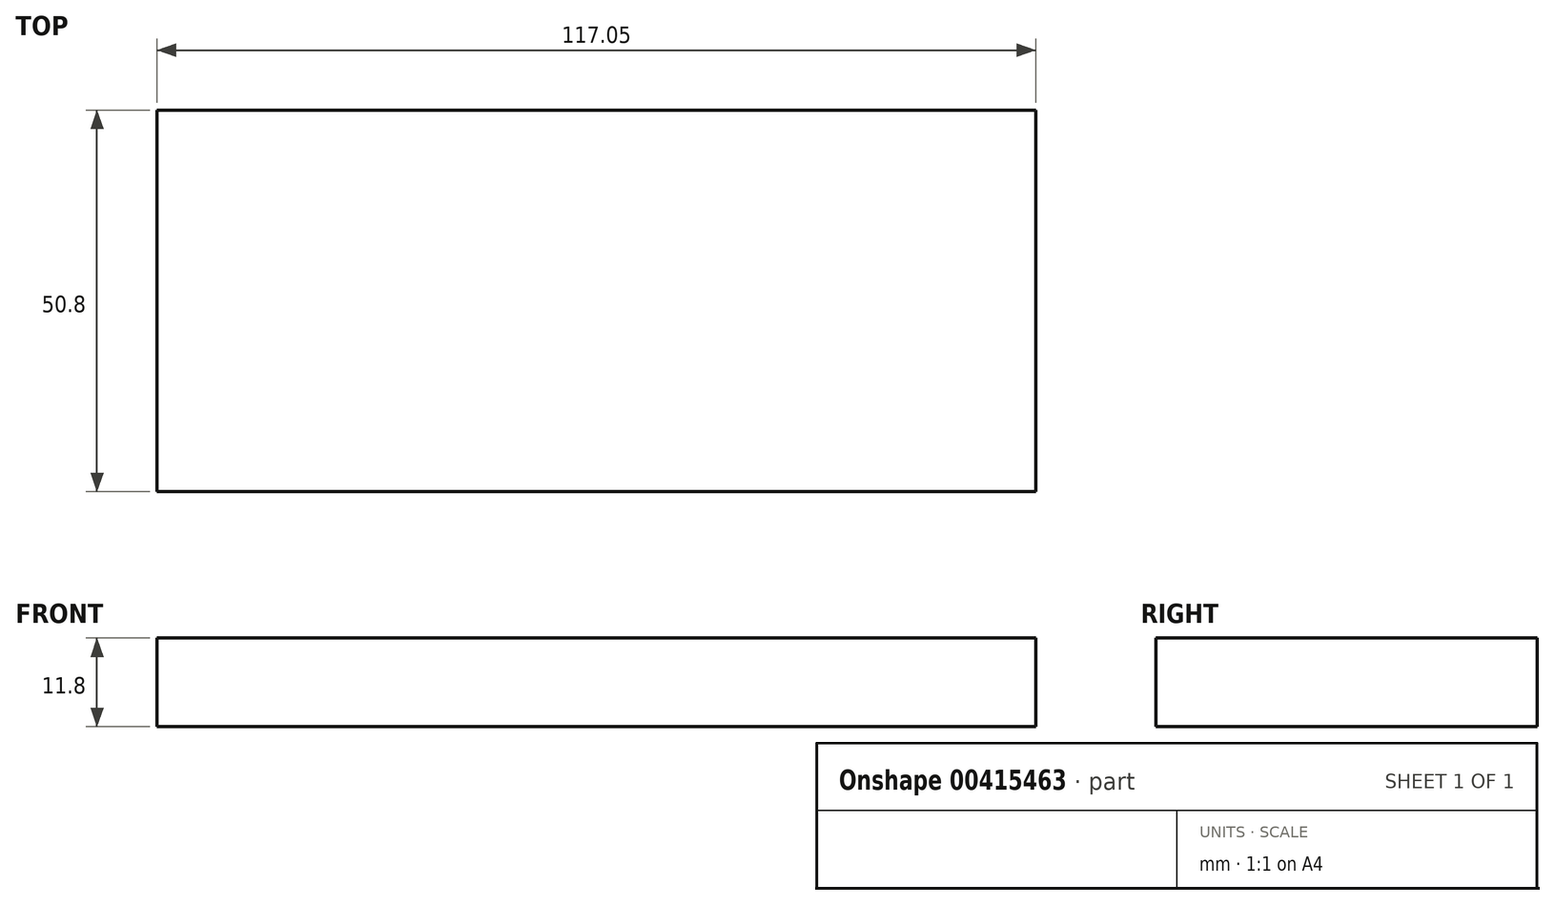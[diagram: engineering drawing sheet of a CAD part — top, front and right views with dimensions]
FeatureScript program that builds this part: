
annotation { "Feature Type Name" : "Feature", "Feature Type Description" : "" }
export const myFeature = defineFeature(function(context is Context, id is Id, definition is map)
    precondition{}
    {
        {
            var Q0;
            Q0=qCreatedBy(makeId("Front.planeOp"),FACE);
            var sketch = newSketch(context, id + "F0", { "sketchPlane" : qUnion([Q0])});
            skLineSegment(sketch, "E0.bottom", {"start": v(-58.15, 119.68) * mm, "end": v(58.9, 119.68) * mm});
            skLineSegment(sketch, "E0.top", {"start": v(-58.15, 131.48) * mm, "end": v(58.9, 131.48) * mm});
            skLineSegment(sketch, "E0.left", {"start": v(-58.15, 119.68) * mm, "end": v(-58.15, 131.48) * mm});
            skLineSegment(sketch, "E0.right", {"start": v(58.9, 119.68) * mm, "end": v(58.9, 131.48) * mm});
            skSolve(sketch);
        }
        {
            var Q0;
            Q0=qSketchRegion(id+"F0",true);
            extrude(context, id + "F1", {"entities" : qUnion([Q0]), "depth" : 50.8 * mm});
        }
    });
